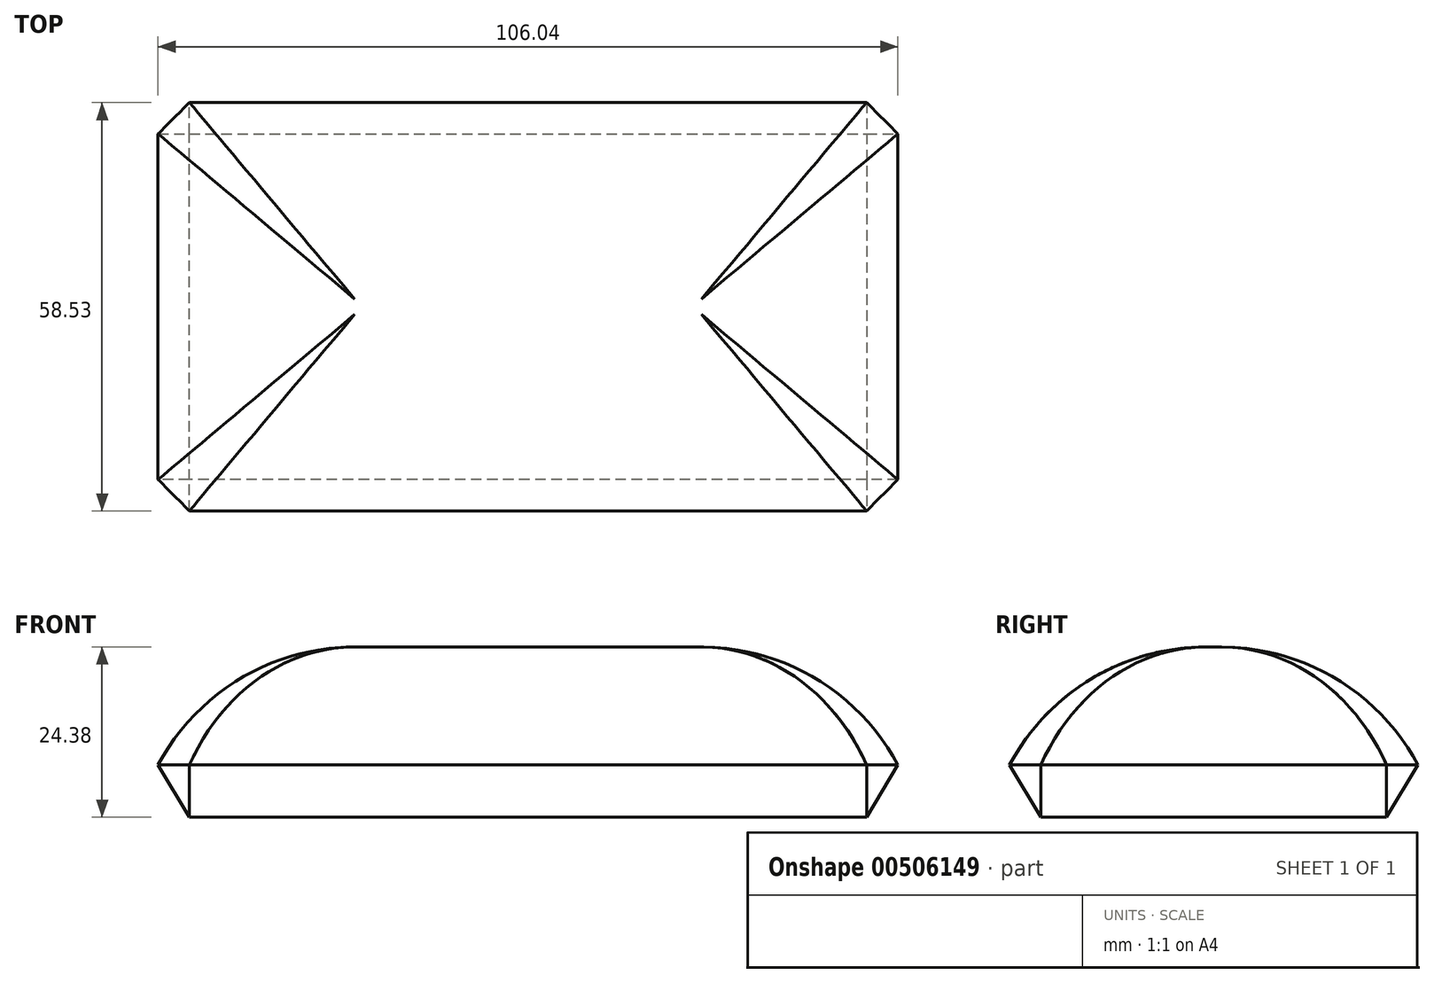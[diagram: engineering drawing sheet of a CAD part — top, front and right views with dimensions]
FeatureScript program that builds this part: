
annotation { "Feature Type Name" : "Feature", "Feature Type Description" : "" }
export const myFeature = defineFeature(function(context is Context, id is Id, definition is map)
    precondition{}
    {
        {
            var Q0;
            Q0=qCreatedBy(makeId("Top.planeOp"),FACE);
            var sketch = newSketch(context, id + "F0", { "sketchPlane" : qUnion([Q0])});
            skLineSegment(sketch, "E0.bottom", {"start": v(-52.82, 28.19) * mm, "end": v(58.89, 28.19) * mm});
            skLineSegment(sketch, "E0.top", {"start": v(-52.82, -36.01) * mm, "end": v(58.89, -36.01) * mm});
            skLineSegment(sketch, "E0.left", {"start": v(-52.82, 28.19) * mm, "end": v(-52.82, -36.01) * mm});
            skLineSegment(sketch, "E0.right", {"start": v(58.89, 28.19) * mm, "end": v(58.89, -36.01) * mm});
            skSolve(sketch);
        }
        {
            var Q0;
            Q0=makeQuery(id+"F0.imprint","IMPRINT",FACE,{"disambiguationData":[TD([[makeQuery(id+"F0.imprint","IMPRINT",EDGE,{"derivedFrom":sQuery(id+"F0.wireOp",EDGE,"E0.bottom")}),-1.0]])]});
            extrude(context, id + "F1", {"entities" : qUnion([Q0]), "endBound" : BoundingType.SYMMETRIC, "depth" : 24.38 * mm});
        }
        {
            var Q0;
            Q0=makeQuery(id+"F1.opExtrude","CAP_FACE",FACE,{"disambiguationData":[OSD([sQuery(id+"F0.wireOp",EDGE,"E0.bottom"),sQuery(id+"F0.wireOp",EDGE,"E0.top"),sQuery(id+"F0.wireOp",EDGE,"E0.left"),sQuery(id+"F0.wireOp",EDGE,"E0.right")])],"isStart":false});
            fillet(context, id + "F2", {"entities" : qUnion([Q0]), "radius" : 31.9 * mm, "tangentPropagation" : true, "allowEdgeOverflow" : false});
        }
        {
            var Q0;
            Q0=makeQuery(id+"F2.opFillet","BLEND_FACE",FACE,{"disambiguationData":[OSD([sQuery(id+"F0.wireOp",EDGE,"E0.top")])]});
            var Q1;
            Q1=makeQuery(id+"F2.opFillet","BLEND_FACE",FACE,{"disambiguationData":[OSD([sQuery(id+"F0.wireOp",EDGE,"E0.right")])]});
            var Q2;
            Q2=makeQuery(id+"F2.opFillet","BLEND_FACE",FACE,{"disambiguationData":[OSD([sQuery(id+"F0.wireOp",EDGE,"E0.bottom")])]});
            var Q3;
            Q3=makeQuery(id+"F2.opFillet","BLEND_FACE",FACE,{"disambiguationData":[OSD([sQuery(id+"F0.wireOp",EDGE,"E0.left")])]});
            chamfer(context, id + "F3", {"entities" : qUnion([Q0, Q1, Q2, Q3]), "width" : 5.08 * mm, "tangentPropagation" : true});
        }
    });
